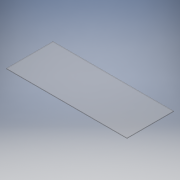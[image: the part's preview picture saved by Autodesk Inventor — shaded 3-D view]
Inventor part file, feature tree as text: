
AUTODESK INVENTOR PART (.ipt)
format: ipt  version: 2016 SP2 (Build 200236200, 236)  size: 104,448 bytes
history: native  units: mm
features: extrude x1, sketch x1
ambient origin geometry x8: Origin, YZ Plane, XZ Plane, XY Plane, X Axis, Y Axis, Z Axis, Center Point
bodies: Volumenkörper1 (feature_tree)
feature tree (2):
  extrude  "Extrusion1"  Depth=153.5mm
  sketch  "Skizze1"  dims[d0=397.6mm d1=153.5mm d2=2.0mm d3=0.0mm]
